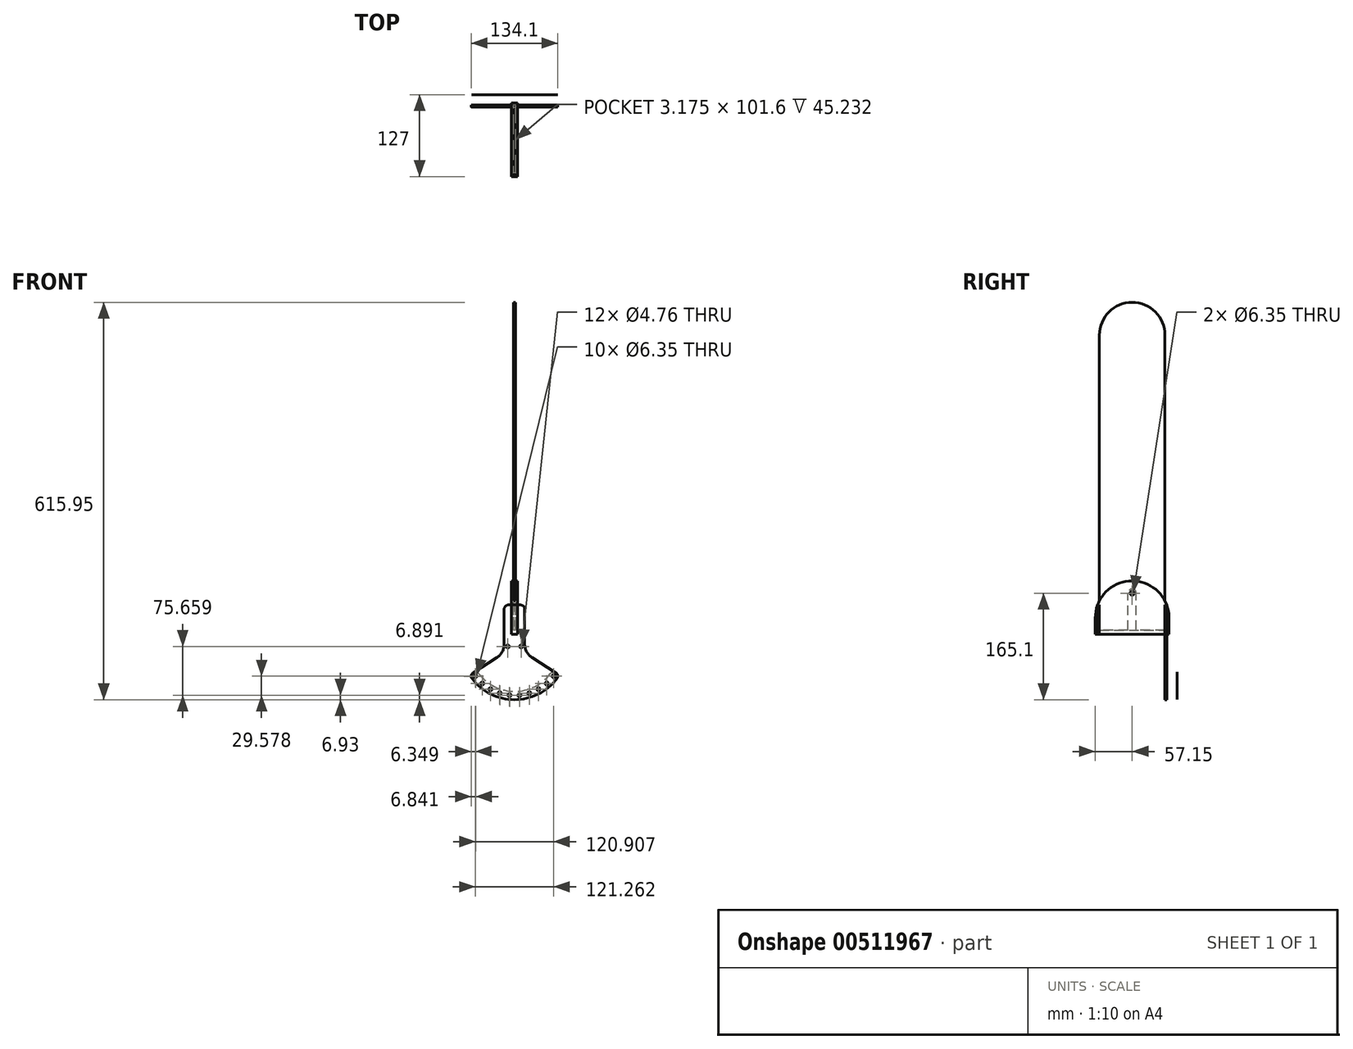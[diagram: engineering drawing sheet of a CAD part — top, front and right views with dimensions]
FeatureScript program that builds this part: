
annotation { "Feature Type Name" : "Feature", "Feature Type Description" : "" }
export const myFeature = defineFeature(function(context is Context, id is Id, definition is map)
    precondition{}
    {
        {
            var Q0;
            Q0=qCreatedBy(makeId("Front.planeOp"),FACE);
            cPlane(context, id + "F0", {"entities" : qUnion([Q0]), "cplaneType" : CPlaneType.OFFSET, "offset" : 101.6 * mm, "width" : 152.4 * mm, "height" : 152.4 * mm});
        }
        {
            var Q0;
            Q0=qCreatedBy(makeId("Front.planeOp"),FACE);
            cPlane(context, id + "F1", {"entities" : qUnion([Q0]), "cplaneType" : CPlaneType.OFFSET, "offset" : 19.05 * mm, "oppositeDirection" : true, "width" : 152.4 * mm, "height" : 152.4 * mm});
        }
        {
            var Q0;
            Q0=qCreatedBy(makeId("Right.planeOp"),FACE);
            var sketch = newSketch(context, id + "F2", { "sketchPlane" : qUnion([Q0])});
            skLineSegment(sketch, "E0", {"start": v(-107.95, 19.05) * mm, "end": v(6.35, 19.05) * mm});
            skCircle(sketch, "E1", {"center": v(-50.8, 82.55) * mm, "radius": 3.18 * mm});
            skLineSegment(sketch, "E2", {"start": v(-107.95, 19.05) * mm, "end": v(-107.95, 44.45) * mm});
            skArc(sketch, "E3", {"start": v(-107.95, 44.45) * mm, "mid": v(-50.8, 101.6) * mm, "end": v(6.35, 44.45) * mm});
            skLineSegment(sketch, "E4", {"start": v(6.35, 44.45) * mm, "end": v(6.35, 19.05) * mm});
            skLineSegment(sketch, "E5", {"start": v(-101.6, 70.63) * mm, "end": v(-101.6, 25.4) * mm});
            skLineSegment(sketch, "E6", {"start": v(-101.6, 25.4) * mm, "end": v(0, 25.4) * mm});
            skLineSegment(sketch, "E7", {"start": v(0, 25.4) * mm, "end": v(0, 70.63) * mm});
            skSolve(sketch);
        }
        {
            var Q0;
            Q0=qCreatedBy(id+"F0.planeOp",FACE);
            var sketch = newSketch(context, id + "F3", { "sketchPlane" : qUnion([Q0])});
            skLineSegment(sketch, "E8.bottom", {"start": v(-9.53, 64.28) * mm, "end": v(9.52, 64.28) * mm});
            skLineSegment(sketch, "E8.top", {"start": v(-9.52, -62.72) * mm, "end": v(9.53, -62.72) * mm});
            skLineSegment(sketch, "E8.left", {"start": v(-15.88, 57.93) * mm, "end": v(-15.88, -56.37) * mm});
            skLineSegment(sketch, "E8.right", {"start": v(15.88, 57.93) * mm, "end": v(15.88, -56.37) * mm});
            skPoint(sketch, "E9.visualSharp", {"position": v(-15.88, 64.28) * mm});
            skArc(sketch, "E9.filletArc", {"start": v(-9.53, 64.28) * mm, "mid": v(-14.02, 62.42) * mm, "end": v(-15.88, 57.93) * mm});
            skPoint(sketch, "E10.visualSharp", {"position": v(15.87, 64.28) * mm});
            skArc(sketch, "E10.filletArc", {"start": v(15.87, 57.93) * mm, "mid": v(14.02, 62.42) * mm, "end": v(9.52, 64.28) * mm});
            skPoint(sketch, "E11.visualSharp", {"position": v(15.88, -62.72) * mm});
            skArc(sketch, "E11.filletArc", {"start": v(9.53, -62.72) * mm, "mid": v(14.02, -60.86) * mm, "end": v(15.88, -56.37) * mm});
            skPoint(sketch, "E12.visualSharp", {"position": v(-15.87, -62.72) * mm});
            skArc(sketch, "E12.filletArc", {"start": v(-15.87, -56.37) * mm, "mid": v(-14.02, -60.86) * mm, "end": v(-9.52, -62.72) * mm});
            skPoint(sketch, "E13", {"position": v(0, 70.63) * mm});
            skCircle(sketch, "E14", {"center": v(-10.32, 0) * mm, "radius": 2.38 * mm});
            skCircle(sketch, "E15", {"center": v(10.32, 0) * mm, "radius": 2.38 * mm});
            skCircle(sketch, "E16.0.1.0", {"center": v(10.32, -29.21) * mm, "radius": 2.38 * mm});
            skCircle(sketch, "E16.0.1.1", {"center": v(-10.32, -29.21) * mm, "radius": 2.38 * mm});
            skCircle(sketch, "E16.0.2.0", {"center": v(10.32, -58.42) * mm, "radius": 2.38 * mm});
            skCircle(sketch, "E16.0.2.1", {"center": v(-10.32, -58.42) * mm, "radius": 2.38 * mm});
            skLineSegment(sketch, "E16.direction1", {"start": v(10.32, 0) * mm, "end": v(-12.03, 0) * mm, "construction": true});
            skLineSegment(sketch, "E16.direction2", {"start": v(10.32, 0) * mm, "end": v(10.32, -29.21) * mm, "construction": true});
            skLineSegment(sketch, "E17.bottom", {"start": v(-4.76, 64.28) * mm, "end": v(-1.59, 64.28) * mm});
            skLineSegment(sketch, "E17.top", {"start": v(-4.76, 19.05) * mm, "end": v(4.76, 19.05) * mm});
            skLineSegment(sketch, "E17.left", {"start": v(-4.76, 64.28) * mm, "end": v(-4.76, 19.05) * mm});
            skLineSegment(sketch, "E18.MirrorCS", {"start": v(4.76, 64.28) * mm, "end": v(4.76, 19.05) * mm});
            skSolve(sketch);
        }
        {
            var Q0;
            Q0=qCreatedBy(makeId("Front.planeOp"),FACE);
            var sketch = newSketch(context, id + "F4", { "sketchPlane" : qUnion([Q0])});
            skPoint(sketch, "E19", {"position": v(-4.76, 19.05) * mm});
            skPoint(sketch, "E20", {"position": v(4.76, 19.05) * mm});
            skPoint(sketch, "E21", {"position": v(4.76, 64.28) * mm});
            skLineSegment(sketch, "E22", {"start": v(-4.76, 19.05) * mm, "end": v(4.76, 19.05) * mm});
            skLineSegment(sketch, "E23", {"start": v(4.76, 64.28) * mm, "end": v(4.76, 19.05) * mm});
            skPoint(sketch, "E24.visualSharp", {"position": v(15.88, 64.28) * mm});
            skPoint(sketch, "E25.newPointB", {"position": v(15.88, -31.75) * mm});
            skLineSegment(sketch, "E26", {"start": v(15.87, 57.93) * mm, "end": v(15.88, 3.82) * mm});
            skLineSegment(sketch, "E27", {"start": v(4.76, 64.28) * mm, "end": v(9.52, 64.28) * mm});
            skArc(sketch, "E28.filletArc", {"start": v(15.88, 57.93) * mm, "mid": v(14.02, 62.42) * mm, "end": v(9.52, 64.28) * mm});
            skCircle(sketch, "E29", {"center": v(-10.32, 0) * mm, "radius": 2.38 * mm});
            skCircle(sketch, "E30", {"center": v(10.32, 0) * mm, "radius": 2.38 * mm});
            skLineSegment(sketch, "E31.MirrorCS", {"start": v(-4.76, 64.28) * mm, "end": v(-4.76, 19.05) * mm});
            skLineSegment(sketch, "E32.MirrorCS", {"start": v(-4.76, 64.28) * mm, "end": v(-9.52, 64.28) * mm});
            skArc(sketch, "E33.MirrorCS", {"start": v(-15.88, 57.93) * mm, "mid": v(-14.02, 62.42) * mm, "end": v(-9.52, 64.28) * mm});
            skPoint(sketch, "E34.visualSharp", {"position": v(15.88, 9.53) * mm});
            skLineSegment(sketch, "E35.MirrorCS", {"start": v(-15.87, 57.93) * mm, "end": v(-15.88, 3.82) * mm});
            skArc(sketch, "E36", {"start": v(-65.68, -50) * mm, "mid": v(0, -82.55) * mm, "end": v(65.68, -50) * mm});
            skLineSegment(sketch, "E37", {"start": v(-64.04, -40.8) * mm, "end": v(-27.63, -17.6) * mm});
            skLineSegment(sketch, "E38", {"start": v(64.04, -40.8) * mm, "end": v(27.63, -17.6) * mm});
            skPoint(sketch, "E39.visualSharp", {"position": v(69.62, -44.35) * mm});
            skArc(sketch, "E39.filletArc", {"start": v(65.68, -50) * mm, "mid": v(66.88, -45.04) * mm, "end": v(64.04, -40.8) * mm});
            skPoint(sketch, "E40.visualSharp", {"position": v(-69.62, -44.35) * mm});
            skArc(sketch, "E40.filletArc", {"start": v(-64.04, -40.8) * mm, "mid": v(-66.88, -45.04) * mm, "end": v(-65.68, -50) * mm});
            skPoint(sketch, "E41.newPointA", {"position": v(-15.88, -10.11) * mm});
            skArc(sketch, "E41.filletArc", {"start": v(-27.63, -17.6) * mm, "mid": v(-19, -8.4) * mm, "end": v(-15.88, 3.82) * mm});
            skPoint(sketch, "E42.newPointA", {"position": v(15.88, -10.11) * mm});
            skArc(sketch, "E42.filletArc", {"start": v(15.88, 3.82) * mm, "mid": v(19, -8.4) * mm, "end": v(27.63, -17.6) * mm});
            skCircle(sketch, "E43", {"center": v(60.63, -46.16) * mm, "radius": 2.38 * mm});
            skCircle(sketch, "E44.1.0", {"center": v(49.97, -57.45) * mm, "radius": 2.38 * mm});
            skCircle(sketch, "E44.2.0", {"center": v(37.25, -66.37) * mm, "radius": 2.38 * mm});
            skCircle(sketch, "E44.3.0", {"center": v(22.98, -72.52) * mm, "radius": 2.38 * mm});
            skCircle(sketch, "E44.4.0", {"center": v(7.77, -75.66) * mm, "radius": 2.38 * mm});
            skCircle(sketch, "E44.5.0", {"center": v(-7.77, -75.66) * mm, "radius": 2.38 * mm});
            skCircle(sketch, "E44.6.0", {"center": v(-22.98, -72.52) * mm, "radius": 2.38 * mm});
            skCircle(sketch, "E44.7.0", {"center": v(-37.25, -66.37) * mm, "radius": 2.38 * mm});
            skCircle(sketch, "E44.8.0", {"center": v(-49.97, -57.45) * mm, "radius": 2.38 * mm});
            skCircle(sketch, "E44.9.0", {"center": v(-60.63, -46.16) * mm, "radius": 2.38 * mm});
            skPoint(sketch, "E44.center", {"position": v(0, 0.37) * mm});
            skLineSegment(sketch, "E44.anchor1", {"start": v(0, 0.37) * mm, "end": v(60.63, -46.16) * mm, "construction": true});
            skLineSegment(sketch, "E44.anchor2", {"start": v(0, 0.37) * mm, "end": v(-60.63, -46.16) * mm, "construction": true});
            skSolve(sketch);
        }
        {
            var Q0;
            Q0=qCreatedBy(id+"F1.planeOp",FACE);
            var sketch = newSketch(context, id + "F5", { "sketchPlane" : qUnion([Q0])});
            skArc(sketch, "E45", {"start": v(-65.17, -50.2) * mm, "mid": v(0.4, -82.35) * mm, "end": v(65.81, -49.9) * mm});
            skPoint(sketch, "E46.visualSharp", {"position": v(69.24, -45.07) * mm});
            skArc(sketch, "E46.filletArc", {"start": v(65.81, -49.9) * mm, "mid": v(64.62, -41) * mm, "end": v(55.72, -42.19) * mm});
            skPoint(sketch, "E47.visualSharp", {"position": v(-68.83, -45.07) * mm});
            skArc(sketch, "E47.filletArc", {"start": v(-55.11, -42.45) * mm, "mid": v(-64.02, -41.3) * mm, "end": v(-65.17, -50.2) * mm});
            skCircle(sketch, "E48", {"center": v(60.77, -46.04) * mm, "radius": 3.18 * mm});
            skCircle(sketch, "E49.1.0", {"center": v(50.16, -57.33) * mm, "radius": 3.18 * mm});
            skCircle(sketch, "E49.2.0", {"center": v(37.5, -66.25) * mm, "radius": 3.18 * mm});
            skCircle(sketch, "E49.3.0", {"center": v(23.29, -72.42) * mm, "radius": 3.18 * mm});
            skCircle(sketch, "E49.4.0", {"center": v(8.13, -75.58) * mm, "radius": 3.18 * mm});
            skCircle(sketch, "E49.5.0", {"center": v(-7.36, -75.62) * mm, "radius": 3.18 * mm});
            skCircle(sketch, "E49.6.0", {"center": v(-22.54, -72.52) * mm, "radius": 3.18 * mm});
            skCircle(sketch, "E49.7.0", {"center": v(-36.77, -66.42) * mm, "radius": 3.18 * mm});
            skCircle(sketch, "E49.8.0", {"center": v(-49.48, -57.57) * mm, "radius": 3.18 * mm});
            skCircle(sketch, "E49.9.0", {"center": v(-60.14, -46.33) * mm, "radius": 3.18 * mm});
            skArc(sketch, "E50", {"start": v(-55.11, -42.45) * mm, "mid": v(0.37, -69.65) * mm, "end": v(55.72, -42.19) * mm});
            skSolve(sketch);
        }
        {
            var Q0;
            {var subQ0=sQuery(id+"F2.wireOp",EDGE,"epXanuwn-nBnr-u1tb-xMDp-uRFG3rdAdBzg");var subQ1=sQuery(id+"F2.wireOp",EDGE,"422123df-42f6-4765-87e8-b6f82bfa0c5e.0");var subQ2=makeQuery(id+"F2.imprint","INTERSECT",VERTEX,{"derivedFrom":[subQ1,subQ0]});Q0=makeQuery(id+"F2.imprint","IMPRINT",FACE,{"disambiguationData":[TD([[makeQuery(id+"F2.imprint","IMPRINT",EDGE,{"disambiguationData":[TD([[subQ2,-1.0]])],"derivedFrom":subQ0}),1.0]])]});}
            var Q1;
            {var subQ0=sQuery(id+"F2.wireOp",EDGE,"ghhASnvt-BqMr-Asl8-nOW3-iuKUiL3CyxJQ.bottom");Q1=makeQuery(id+"F2.imprint","IMPRINT",FACE,{"disambiguationData":[TD([[makeQuery(id+"F2.imprint","IMPRINT",EDGE,{"derivedFrom":subQ0}),-1.0]])]});}
            var Q2;
            {var subQ5=sQuery(id+"F2.wireOp",EDGE,"bc79e0f3-8f85-4b2a-9bf4-085f16866aeb.0");Q2=makeQuery(id+"F2.imprint","IMPRINT",FACE,{"disambiguationData":[TD([[makeQuery(id+"F2.imprint","IMPRINT",EDGE,{"derivedFrom":subQ5}),1.0]])]});}
            var Q3;
            {var subQ0=sQuery(id+"F2.wireOp",EDGE,"JBdrXrEb-KRSL-1iJ1-4eLd-cI5kpoJfhlAo.bottom");Q3=makeQuery(id+"F2.imprint","IMPRINT",FACE,{"disambiguationData":[TD([[makeQuery(id+"F2.imprint","IMPRINT",EDGE,{"derivedFrom":subQ0}),-1.0]])]});}
            var Q4;
            {var subQ0=sQuery(id+"F2.wireOp",EDGE,"E0");var subQ1=sQuery(id+"F2.wireOp",EDGE,"422123df-42f6-4765-87e8-b6f82bfa0c5e.0");var subQ2=makeQuery(id+"F2.imprint","INTERSECT",VERTEX,{"derivedFrom":[subQ1,subQ0]});Q4=makeQuery(id+"F2.imprint","IMPRINT",FACE,{"disambiguationData":[TD([[makeQuery(id+"F2.imprint","IMPRINT",EDGE,{"disambiguationData":[TD([[subQ2,1.0]])],"derivedFrom":subQ0}),1.0]])]});}
            var Q5;
            Q5=makeQuery(id+"F2.imprint","IMPRINT",FACE,{"disambiguationData":[TD([[makeQuery(id+"F2.imprint","IMPRINT",EDGE,{"derivedFrom":sQuery(id+"F2.wireOp",EDGE,"E1")}),-1.0]])]});
            extrude(context, id + "F6", {"entities" : qUnion([Q0, Q1, Q2, Q3, Q4, Q5]), "endBound" : BoundingType.SYMMETRIC, "depth" : 9.52 * mm, "offsetDistance" : 25.4 * mm});
        }
        {
            var Q0;
            Q0=makeQuery(id+"F2.imprint","IMPRINT",FACE,{"disambiguationData":[TD([[makeQuery(id+"F2.imprint","IMPRINT",EDGE,{"derivedFrom":sQuery(id+"F2.wireOp",EDGE,"E1")}),-1.0]])]});
            extrude(context, id + "F7", {"entities" : qUnion([Q0]), "operationType" : NewBodyOperationType.REMOVE, "endBound" : BoundingType.SYMMETRIC, "depth" : 3.17 * mm, "offsetDistance" : 25.4 * mm});
        }
        {
            var Q0;
            Q0=makeQuery(id+"F3.imprint","IMPRINT",FACE,{"disambiguationData":[TD([[makeQuery(id+"F3.imprint","IMPRINT",EDGE,{"derivedFrom":sQuery(id+"F3.wireOp",EDGE,"E8.bottom")}),-1.0]])]});
            extrude(context, id + "F8", {"entities" : qUnion([Q0]), "depth" : 3.17 * mm});
        }
        {
            var Q0;
            Q0=makeQuery(id+"F4.imprint","IMPRINT",FACE,{"disambiguationData":[TD([[makeQuery(id+"F4.imprint","IMPRINT",EDGE,{"derivedFrom":sQuery(id+"F4.wireOp",EDGE,"E22")}),-1.0]])]});
            var Q1;
            {var subQ0=sQuery(id+"F4.wireOp",EDGE,"c9da0bad-71dc-4ab2-be7a-5dc441e94ecf0.MirrorCS");var subQ1=sQuery(id+"F4.wireOp",EDGE,"F5ZkB9Hz-F5qx-JeGK-KaSx-McvdkS8WqKVC");var subQ2=makeQuery(id+"F4.imprint","INTERSECT",VERTEX,{"derivedFrom":[subQ1,subQ0]});Q1=makeQuery(id+"F4.imprint","IMPRINT",FACE,{"disambiguationData":[TD([[makeQuery(id+"F4.imprint","IMPRINT",EDGE,{"disambiguationData":[TD([[subQ2,1.0]])],"derivedFrom":subQ1}),1.0]])]});}
            var Q2;
            Q2=makeQuery(id+"F4.imprint","IMPRINT",FACE,{"disambiguationData":[TD([[makeQuery(id+"F4.imprint","IMPRINT",EDGE,{"derivedFrom":sQuery(id+"F4.wireOp",EDGE,"E36")}),1.0]])]});
            extrude(context, id + "F9", {"entities" : qUnion([Q0, Q1, Q2]), "oppositeDirection" : true, "depth" : 3.17 * mm, "offsetDistance" : 25.4 * mm});
        }
        {
            var Q0;
            Q0=makeQuery(id+"F5.imprint","IMPRINT",FACE,{"disambiguationData":[TD([[makeQuery(id+"F5.imprint","IMPRINT",EDGE,{"derivedFrom":sQuery(id+"F5.wireOp",EDGE,"E45")}),1.0]])]});
            extrude(context, id + "F10", {"entities" : qUnion([Q0]), "depth" : 1 / 203.2 * mm, "offsetDistance" : 25.4 * mm});
        }
        {
            var Q0;
            Q0=qCreatedBy(makeId("Right.planeOp"),FACE);
            var sketch = newSketch(context, id + "F11", { "sketchPlane" : qUnion([Q0])});
            skLineSegment(sketch, "E51", {"start": v(-101.6, 25.4) * mm, "end": v(-101.6, 482.6) * mm});
            skLineSegment(sketch, "E52", {"start": v(0, 482.6) * mm, "end": v(0, 25.4) * mm});
            skLineSegment(sketch, "E53", {"start": v(0, 25.4) * mm, "end": v(-101.6, 25.4) * mm});
            skCircle(sketch, "E54", {"center": v(-50.8, 82.55) * mm, "radius": 6.35 * mm});
            skLineSegment(sketch, "E55", {"start": v(-44.45, 25.4) * mm, "end": v(-44.45, 82.55) * mm});
            skLineSegment(sketch, "E56", {"start": v(-57.15, 25.4) * mm, "end": v(-57.15, 82.55) * mm});
            skArc(sketch, "E57", {"start": v(0, 482.6) * mm, "mid": v(-50.8, 533.4) * mm, "end": v(-101.6, 482.6) * mm});
            skSolve(sketch);
        }
        {
            var Q0;
            {var subQ1=sQuery(id+"F11.wireOp",EDGE,"E51");Q0=makeQuery(id+"F11.imprint","IMPRINT",FACE,{"disambiguationData":[TD([[makeQuery(id+"F11.imprint","IMPRINT",EDGE,{"derivedFrom":subQ1}),-1.0]])]});}
            extrude(context, id + "F12", {"entities" : qUnion([Q0]), "endBound" : BoundingType.SYMMETRIC, "depth" : 3.17 * mm, "offsetDistance" : 25.4 * mm});
        }
    });
